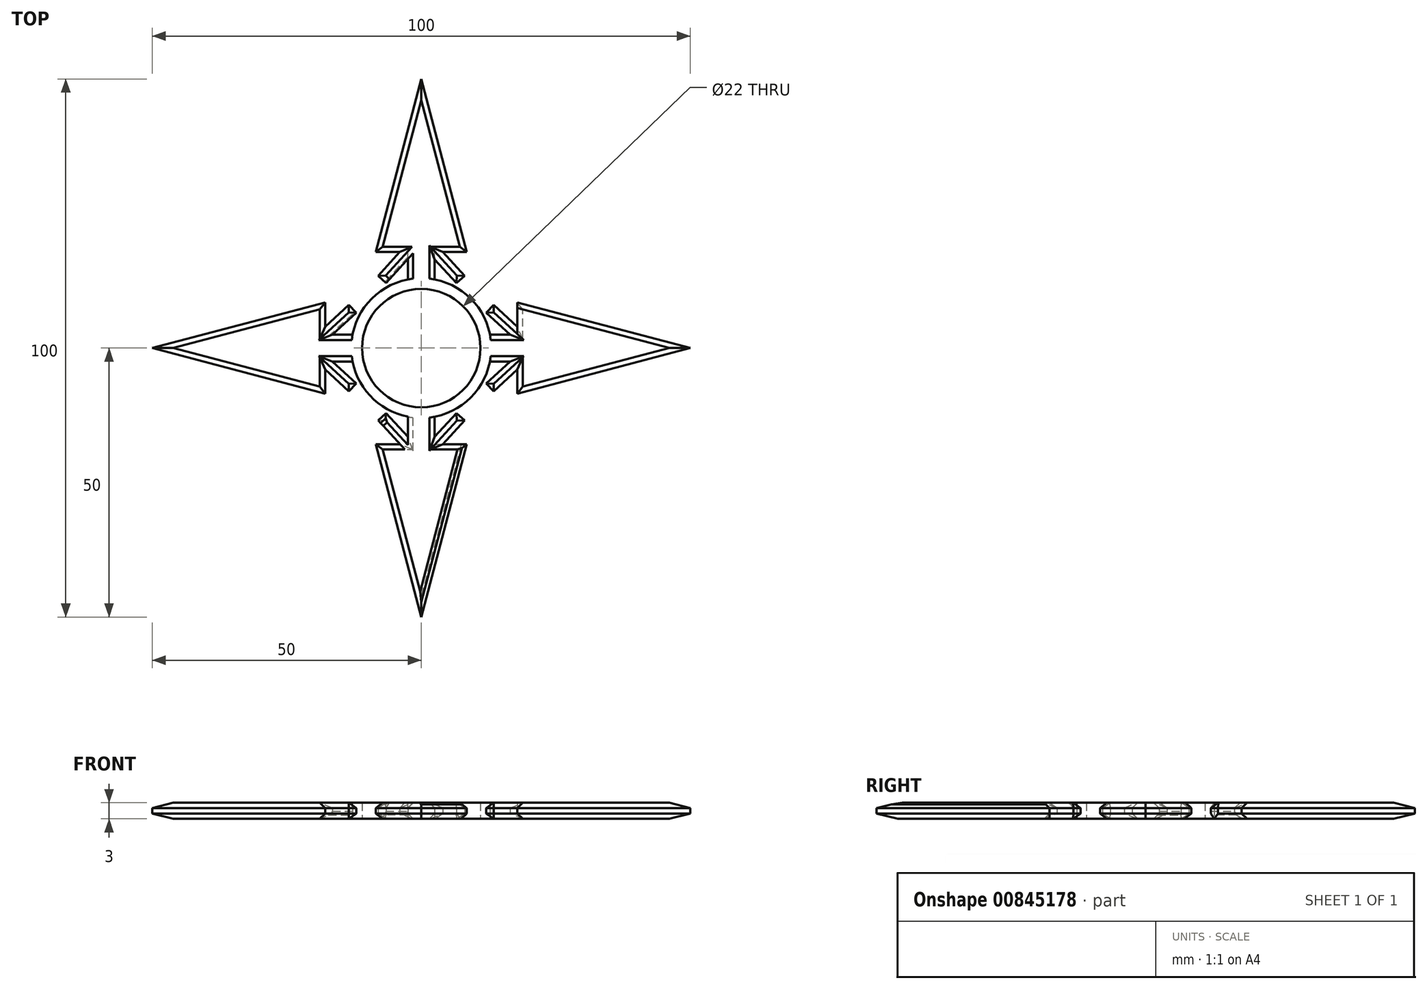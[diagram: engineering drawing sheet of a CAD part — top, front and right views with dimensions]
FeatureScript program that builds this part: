
annotation { "Feature Type Name" : "Feature", "Feature Type Description" : "" }
export const myFeature = defineFeature(function(context is Context, id is Id, definition is map)
    precondition{}
    {
        {
            var Q0;
            Q0=qCreatedBy(makeId("Top.planeOp"),FACE);
            var sketch = newSketch(context, id + "F0", { "sketchPlane" : qUnion([Q0])});
            skArc(sketch, "E0", {"start": v(7.78, 7.78) * mm, "mid": v(0, 11) * mm, "end": v(-7.78, 7.78) * mm});
            skArc(sketch, "E1", {"start": v(9.2, 9.2) * mm, "mid": v(6.11, 11.47) * mm, "end": v(2.5, 12.76) * mm});
            skLineSegment(sketch, "E2", {"start": v(0, 0) * mm, "end": v(0, 50) * mm});
            skLineSegment(sketch, "E3", {"start": v(0, 0) * mm, "end": v(-2.5, 0) * mm});
            skLineSegment(sketch, "E4", {"start": v(0, 0) * mm, "end": v(2.5, 0) * mm});
            skLineSegment(sketch, "E5", {"start": v(-2.5, 12.76) * mm, "end": v(-2.5, 16.5) * mm});
            skLineSegment(sketch, "E6", {"start": v(2.5, 12.76) * mm, "end": v(2.5, 16.5) * mm});
            skLineSegment(sketch, "E7", {"start": v(-2.5, 16.5) * mm, "end": v(-6.56, 12.08) * mm});
            skLineSegment(sketch, "E8", {"start": v(-6.56, 12.08) * mm, "end": v(-8.03, 13.43) * mm});
            skLineSegment(sketch, "E9", {"start": v(-8.03, 13.43) * mm, "end": v(-3.97, 17.85) * mm});
            skLineSegment(sketch, "E10", {"start": v(-3.97, 17.85) * mm, "end": v(-8.47, 17.85) * mm});
            skLineSegment(sketch, "E11", {"start": v(-8.47, 17.85) * mm, "end": v(0, 50) * mm});
            skLineSegment(sketch, "E12.MirrorCS", {"start": v(2.5, 16.5) * mm, "end": v(6.56, 12.08) * mm});
            skLineSegment(sketch, "E13.MirrorCS", {"start": v(8.03, 13.43) * mm, "end": v(3.97, 17.85) * mm});
            skLineSegment(sketch, "E14.MirrorCS", {"start": v(6.56, 12.08) * mm, "end": v(8.03, 13.43) * mm});
            skLineSegment(sketch, "E15.MirrorCS", {"start": v(3.97, 17.85) * mm, "end": v(8.47, 17.85) * mm});
            skLineSegment(sketch, "E16.MirrorCS", {"start": v(8.47, 17.85) * mm, "end": v(0, 50) * mm});
            skArc(sketch, "E17.trimOffspring", {"start": v(-2.5, 12.76) * mm, "mid": v(-6.11, 11.47) * mm, "end": v(-9.2, 9.2) * mm});
            skLineSegment(sketch, "E18.1.0", {"start": v(-13.43, 8.03) * mm, "end": v(-17.85, 3.97) * mm});
            skLineSegment(sketch, "E18.1.1", {"start": v(-17.85, 3.97) * mm, "end": v(-17.85, 8.47) * mm});
            skLineSegment(sketch, "E18.1.2", {"start": v(0, 0) * mm, "end": v(-50, 0) * mm});
            skArc(sketch, "E18.1.3", {"start": v(-7.78, 7.78) * mm, "mid": v(-11, 0) * mm, "end": v(-7.78, -7.78) * mm});
            skLineSegment(sketch, "E18.1.4", {"start": v(-17.85, -3.97) * mm, "end": v(-17.85, -8.47) * mm});
            skLineSegment(sketch, "E18.1.5", {"start": v(-17.85, -8.47) * mm, "end": v(-50, 0) * mm});
            skLineSegment(sketch, "E18.1.6", {"start": v(-16.5, 2.5) * mm, "end": v(-12.08, 6.56) * mm});
            skLineSegment(sketch, "E18.1.7", {"start": v(-17.85, 8.47) * mm, "end": v(-50, 0) * mm});
            skArc(sketch, "E18.1.8", {"start": v(-9.2, 9.2) * mm, "mid": v(-11.47, 6.11) * mm, "end": v(-12.76, 2.5) * mm});
            skLineSegment(sketch, "E18.1.9", {"start": v(0, 0) * mm, "end": v(0, -2.5) * mm});
            skLineSegment(sketch, "E18.1.10", {"start": v(0, 0) * mm, "end": v(0, 2.5) * mm});
            skArc(sketch, "E18.1.11", {"start": v(-12.76, -2.5) * mm, "mid": v(-11.47, -6.11) * mm, "end": v(-9.2, -9.2) * mm});
            skLineSegment(sketch, "E18.1.12", {"start": v(-13.43, -8.03) * mm, "end": v(-17.85, -3.97) * mm});
            skLineSegment(sketch, "E18.1.13", {"start": v(-16.5, -2.5) * mm, "end": v(-12.08, -6.56) * mm});
            skLineSegment(sketch, "E18.1.14", {"start": v(-12.08, 6.56) * mm, "end": v(-13.43, 8.03) * mm});
            skLineSegment(sketch, "E18.1.15", {"start": v(-12.76, 2.5) * mm, "end": v(-16.5, 2.5) * mm});
            skLineSegment(sketch, "E18.1.16", {"start": v(-12.08, -6.56) * mm, "end": v(-13.43, -8.03) * mm});
            skLineSegment(sketch, "E18.1.17", {"start": v(-12.76, -2.5) * mm, "end": v(-16.5, -2.5) * mm});
            skLineSegment(sketch, "E18.2.0", {"start": v(-8.03, -13.43) * mm, "end": v(-3.97, -17.85) * mm});
            skLineSegment(sketch, "E18.2.1", {"start": v(-3.97, -17.85) * mm, "end": v(-8.47, -17.85) * mm});
            skLineSegment(sketch, "E18.2.2", {"start": v(0, 0) * mm, "end": v(0, -50) * mm});
            skArc(sketch, "E18.2.3", {"start": v(-7.78, -7.78) * mm, "mid": v(0, -11) * mm, "end": v(7.78, -7.78) * mm});
            skLineSegment(sketch, "E18.2.4", {"start": v(3.97, -17.85) * mm, "end": v(8.47, -17.85) * mm});
            skLineSegment(sketch, "E18.2.5", {"start": v(8.47, -17.85) * mm, "end": v(0, -50) * mm});
            skLineSegment(sketch, "E18.2.6", {"start": v(-2.5, -16.5) * mm, "end": v(-6.56, -12.08) * mm});
            skLineSegment(sketch, "E18.2.7", {"start": v(-8.47, -17.85) * mm, "end": v(0, -50) * mm});
            skArc(sketch, "E18.2.8", {"start": v(-9.2, -9.2) * mm, "mid": v(-6.11, -11.47) * mm, "end": v(-2.5, -12.76) * mm});
            skArc(sketch, "E18.2.11", {"start": v(2.5, -12.76) * mm, "mid": v(6.11, -11.47) * mm, "end": v(9.2, -9.2) * mm});
            skLineSegment(sketch, "E18.2.12", {"start": v(8.03, -13.43) * mm, "end": v(3.97, -17.85) * mm});
            skLineSegment(sketch, "E18.2.13", {"start": v(2.5, -16.5) * mm, "end": v(6.56, -12.08) * mm});
            skLineSegment(sketch, "E18.2.14", {"start": v(-6.56, -12.08) * mm, "end": v(-8.03, -13.43) * mm});
            skLineSegment(sketch, "E18.2.15", {"start": v(-2.5, -12.76) * mm, "end": v(-2.5, -16.5) * mm});
            skLineSegment(sketch, "E18.2.16", {"start": v(6.56, -12.08) * mm, "end": v(8.03, -13.43) * mm});
            skLineSegment(sketch, "E18.2.17", {"start": v(2.5, -12.76) * mm, "end": v(2.5, -16.5) * mm});
            skLineSegment(sketch, "E18.3.0", {"start": v(13.43, -8.03) * mm, "end": v(17.85, -3.97) * mm});
            skLineSegment(sketch, "E18.3.1", {"start": v(17.85, -3.97) * mm, "end": v(17.85, -8.47) * mm});
            skLineSegment(sketch, "E18.3.2", {"start": v(0, 0) * mm, "end": v(50, 0) * mm});
            skArc(sketch, "E18.3.3", {"start": v(7.78, -7.78) * mm, "mid": v(11, 0) * mm, "end": v(7.78, 7.78) * mm});
            skLineSegment(sketch, "E18.3.4", {"start": v(17.85, 3.97) * mm, "end": v(17.85, 8.47) * mm});
            skLineSegment(sketch, "E18.3.5", {"start": v(17.85, 8.47) * mm, "end": v(50, 0) * mm});
            skLineSegment(sketch, "E18.3.6", {"start": v(16.5, -2.5) * mm, "end": v(12.08, -6.56) * mm});
            skLineSegment(sketch, "E18.3.7", {"start": v(17.85, -8.47) * mm, "end": v(50, 0) * mm});
            skArc(sketch, "E18.3.8", {"start": v(9.2, -9.2) * mm, "mid": v(11.47, -6.11) * mm, "end": v(12.76, -2.5) * mm});
            skLineSegment(sketch, "E18.3.9", {"start": v(0, 0) * mm, "end": v(0, 2.5) * mm});
            skLineSegment(sketch, "E18.3.10", {"start": v(0, 0) * mm, "end": v(0, -2.5) * mm});
            skArc(sketch, "E18.3.11", {"start": v(12.76, 2.5) * mm, "mid": v(11.47, 6.11) * mm, "end": v(9.2, 9.2) * mm});
            skLineSegment(sketch, "E18.3.12", {"start": v(13.43, 8.03) * mm, "end": v(17.85, 3.97) * mm});
            skLineSegment(sketch, "E18.3.13", {"start": v(16.5, 2.5) * mm, "end": v(12.08, 6.56) * mm});
            skLineSegment(sketch, "E18.3.14", {"start": v(12.08, -6.56) * mm, "end": v(13.43, -8.03) * mm});
            skLineSegment(sketch, "E18.3.15", {"start": v(12.76, -2.5) * mm, "end": v(16.5, -2.5) * mm});
            skLineSegment(sketch, "E18.3.16", {"start": v(12.08, 6.56) * mm, "end": v(13.43, 8.03) * mm});
            skLineSegment(sketch, "E18.3.17", {"start": v(12.76, 2.5) * mm, "end": v(16.5, 2.5) * mm});
            skSolve(sketch);
        }
        {
            var Q0;
            Q0 = qSketchRegion(id + "F0", true);
            extrude(context, id + "F1", {"entities" : qUnion([Q0]), "depth" : 3 * mm, "offsetDistance" : 25 * mm});
        }
        {
            var Q0;
            Q0=makeQuery(id+"F1.opExtrude","CAP_EDGE",EDGE,{"disambiguationData":[OSD([sQuery(id+"F0.wireOp",EDGE,"E11")])],"isStart":false});
            var Q1;
            Q1=makeQuery(id+"F1.opExtrude","CAP_EDGE",EDGE,{"disambiguationData":[OSD([sQuery(id+"F0.wireOp",EDGE,"E18.1.7")])],"isStart":false});
            var Q2;
            Q2=makeQuery(id+"F1.opExtrude","CAP_EDGE",EDGE,{"disambiguationData":[OSD([sQuery(id+"F0.wireOp",EDGE,"E18.1.5")])],"isStart":false});
            var Q3;
            Q3=makeQuery(id+"F1.opExtrude","CAP_EDGE",EDGE,{"disambiguationData":[OSD([sQuery(id+"F0.wireOp",EDGE,"E18.2.5")])],"isStart":false});
            var Q4;
            Q4=makeQuery(id+"F1.opExtrude","CAP_EDGE",EDGE,{"disambiguationData":[OSD([sQuery(id+"F0.wireOp",EDGE,"E18.2.7")])],"isStart":false});
            var Q5;
            Q5=makeQuery(id+"F1.opExtrude","CAP_EDGE",EDGE,{"disambiguationData":[OSD([sQuery(id+"F0.wireOp",EDGE,"E18.3.7")])],"isStart":false});
            var Q6;
            Q6=makeQuery(id+"F1.opExtrude","CAP_EDGE",EDGE,{"disambiguationData":[OSD([sQuery(id+"F0.wireOp",EDGE,"E18.3.5")])],"isStart":false});
            var Q7;
            Q7=makeQuery(id+"F1.opExtrude","CAP_EDGE",EDGE,{"disambiguationData":[OSD([sQuery(id+"F0.wireOp",EDGE,"E16.MirrorCS")])],"isStart":false});
            chamfer(context, id + "F2", {"entities" : qUnion([Q0, Q1, Q2, Q3, Q4, Q5, Q6, Q7]), "width" : 1 * mm, "tangentPropagation" : true});
        }
        {
            var Q0;
            Q0=makeQuery(id+"F1.opExtrude","CAP_EDGE",EDGE,{"disambiguationData":[OSD([sQuery(id+"F0.wireOp",EDGE,"E16.MirrorCS")])],"isStart":true});
            var Q1;
            Q1=makeQuery(id+"F1.opExtrude","CAP_EDGE",EDGE,{"disambiguationData":[OSD([sQuery(id+"F0.wireOp",EDGE,"E11")])],"isStart":true});
            var Q2;
            Q2=makeQuery(id+"F1.opExtrude","CAP_EDGE",EDGE,{"disambiguationData":[OSD([sQuery(id+"F0.wireOp",EDGE,"E18.3.7")])],"isStart":true});
            var Q3;
            Q3=makeQuery(id+"F1.opExtrude","CAP_EDGE",EDGE,{"disambiguationData":[OSD([sQuery(id+"F0.wireOp",EDGE,"E18.3.5")])],"isStart":true});
            var Q4;
            Q4=makeQuery(id+"F1.opExtrude","CAP_EDGE",EDGE,{"disambiguationData":[OSD([sQuery(id+"F0.wireOp",EDGE,"E18.2.5")])],"isStart":true});
            var Q5;
            Q5=makeQuery(id+"F1.opExtrude","CAP_EDGE",EDGE,{"disambiguationData":[OSD([sQuery(id+"F0.wireOp",EDGE,"E18.2.7")])],"isStart":true});
            var Q6;
            Q6=makeQuery(id+"F1.opExtrude","CAP_EDGE",EDGE,{"disambiguationData":[OSD([sQuery(id+"F0.wireOp",EDGE,"E18.1.5")])],"isStart":true});
            var Q7;
            Q7=makeQuery(id+"F1.opExtrude","CAP_EDGE",EDGE,{"disambiguationData":[OSD([sQuery(id+"F0.wireOp",EDGE,"E18.1.7")])],"isStart":true});
            var Q8;
            Q8=makeQuery(id+"F1.opExtrude","CAP_EDGE",EDGE,{"disambiguationData":[OSD([sQuery(id+"F0.wireOp",EDGE,"E13.MirrorCS")])],"isStart":true});
            var Q9;
            Q9=makeQuery(id+"F1.opExtrude","CAP_EDGE",EDGE,{"disambiguationData":[OSD([sQuery(id+"F0.wireOp",EDGE,"E12.MirrorCS")])],"isStart":true});
            var Q10;
            Q10=makeQuery(id+"F1.opExtrude","CAP_EDGE",EDGE,{"disambiguationData":[OSD([sQuery(id+"F0.wireOp",EDGE,"E7")])],"isStart":true});
            var Q11;
            Q11=makeQuery(id+"F1.opExtrude","CAP_EDGE",EDGE,{"disambiguationData":[OSD([sQuery(id+"F0.wireOp",EDGE,"E9")])],"isStart":true});
            var Q12;
            Q12=makeQuery(id+"F1.opExtrude","CAP_EDGE",EDGE,{"disambiguationData":[OSD([sQuery(id+"F0.wireOp",EDGE,"E10")])],"isStart":true});
            var Q13;
            Q13=makeQuery(id+"F1.opExtrude","CAP_EDGE",EDGE,{"disambiguationData":[OSD([sQuery(id+"F0.wireOp",EDGE,"E15.MirrorCS")])],"isStart":true});
            var Q14;
            Q14=makeQuery(id+"F1.opExtrude","CAP_EDGE",EDGE,{"disambiguationData":[OSD([sQuery(id+"F0.wireOp",EDGE,"E18.3.13")])],"isStart":true});
            var Q15;
            Q15=makeQuery(id+"F1.opExtrude","CAP_EDGE",EDGE,{"disambiguationData":[OSD([sQuery(id+"F0.wireOp",EDGE,"E18.3.12")])],"isStart":true});
            var Q16;
            Q16=makeQuery(id+"F1.opExtrude","CAP_EDGE",EDGE,{"disambiguationData":[OSD([sQuery(id+"F0.wireOp",EDGE,"E18.3.4")])],"isStart":true});
            var Q17;
            Q17=makeQuery(id+"F1.opExtrude","CAP_EDGE",EDGE,{"disambiguationData":[OSD([sQuery(id+"F0.wireOp",EDGE,"E18.3.16")])],"isStart":true});
            var Q18;
            Q18=makeQuery(id+"F1.opExtrude","CAP_EDGE",EDGE,{"disambiguationData":[OSD([sQuery(id+"F0.wireOp",EDGE,"E18.3.0")])],"isStart":true});
            var Q19;
            Q19=makeQuery(id+"F1.opExtrude","CAP_EDGE",EDGE,{"disambiguationData":[OSD([sQuery(id+"F0.wireOp",EDGE,"E18.3.1")])],"isStart":true});
            var Q20;
            Q20=makeQuery(id+"F1.opExtrude","CAP_EDGE",EDGE,{"disambiguationData":[OSD([sQuery(id+"F0.wireOp",EDGE,"E18.3.6")])],"isStart":true});
            var Q21;
            Q21=makeQuery(id+"F1.opExtrude","CAP_EDGE",EDGE,{"disambiguationData":[OSD([sQuery(id+"F0.wireOp",EDGE,"E18.3.14")])],"isStart":true});
            var Q22;
            Q22=makeQuery(id+"F1.opExtrude","CAP_EDGE",EDGE,{"disambiguationData":[OSD([sQuery(id+"F0.wireOp",EDGE,"E18.3.15")])],"isStart":true});
            var Q23;
            Q23=makeQuery(id+"F1.opExtrude","CAP_EDGE",EDGE,{"disambiguationData":[OSD([sQuery(id+"F0.wireOp",EDGE,"E18.3.17")])],"isStart":true});
            var Q24;
            Q24=makeQuery(id+"F1.opExtrude","CAP_EDGE",EDGE,{"disambiguationData":[OSD([sQuery(id+"F0.wireOp",EDGE,"E18.2.12")])],"isStart":true});
            var Q25;
            Q25=makeQuery(id+"F1.opExtrude","CAP_EDGE",EDGE,{"disambiguationData":[OSD([sQuery(id+"F0.wireOp",EDGE,"E18.2.16")])],"isStart":true});
            var Q26;
            Q26=makeQuery(id+"F1.opExtrude","CAP_EDGE",EDGE,{"disambiguationData":[OSD([sQuery(id+"F0.wireOp",EDGE,"E18.2.13")])],"isStart":true});
            var Q27;
            Q27=makeQuery(id+"F1.opExtrude","CAP_EDGE",EDGE,{"disambiguationData":[OSD([sQuery(id+"F0.wireOp",EDGE,"E18.2.17")])],"isStart":true});
            var Q28;
            Q28=makeQuery(id+"F1.opExtrude","CAP_EDGE",EDGE,{"disambiguationData":[OSD([sQuery(id+"F0.wireOp",EDGE,"E18.2.15")])],"isStart":true});
            var Q29;
            Q29=makeQuery(id+"F1.opExtrude","CAP_EDGE",EDGE,{"disambiguationData":[OSD([sQuery(id+"F0.wireOp",EDGE,"E18.2.6")])],"isStart":true});
            var Q30;
            Q30=makeQuery(id+"F1.opExtrude","CAP_EDGE",EDGE,{"disambiguationData":[OSD([sQuery(id+"F0.wireOp",EDGE,"E18.2.14")])],"isStart":true});
            var Q31;
            Q31=makeQuery(id+"F1.opExtrude","CAP_EDGE",EDGE,{"disambiguationData":[OSD([sQuery(id+"F0.wireOp",EDGE,"E18.2.0")])],"isStart":true});
            var Q32;
            Q32=makeQuery(id+"F1.opExtrude","CAP_EDGE",EDGE,{"disambiguationData":[OSD([sQuery(id+"F0.wireOp",EDGE,"E18.2.1")])],"isStart":true});
            var Q33;
            Q33=makeQuery(id+"F1.opExtrude","CAP_EDGE",EDGE,{"disambiguationData":[OSD([sQuery(id+"F0.wireOp",EDGE,"E18.1.4")])],"isStart":true});
            var Q34;
            Q34=makeQuery(id+"F1.opExtrude","CAP_EDGE",EDGE,{"disambiguationData":[OSD([sQuery(id+"F0.wireOp",EDGE,"E18.1.12")])],"isStart":true});
            var Q35;
            Q35=makeQuery(id+"F1.opExtrude","CAP_EDGE",EDGE,{"disambiguationData":[OSD([sQuery(id+"F0.wireOp",EDGE,"E18.1.16")])],"isStart":true});
            var Q36;
            Q36=makeQuery(id+"F1.opExtrude","CAP_EDGE",EDGE,{"disambiguationData":[OSD([sQuery(id+"F0.wireOp",EDGE,"E18.1.13")])],"isStart":true});
            var Q37;
            Q37=makeQuery(id+"F1.opExtrude","CAP_EDGE",EDGE,{"disambiguationData":[OSD([sQuery(id+"F0.wireOp",EDGE,"E18.1.17")])],"isStart":true});
            var Q38;
            Q38=makeQuery(id+"F1.opExtrude","CAP_EDGE",EDGE,{"disambiguationData":[OSD([sQuery(id+"F0.wireOp",EDGE,"E18.1.15")])],"isStart":true});
            var Q39;
            Q39=makeQuery(id+"F1.opExtrude","CAP_EDGE",EDGE,{"disambiguationData":[OSD([sQuery(id+"F0.wireOp",EDGE,"E18.1.6")])],"isStart":true});
            var Q40;
            Q40=makeQuery(id+"F1.opExtrude","CAP_EDGE",EDGE,{"disambiguationData":[OSD([sQuery(id+"F0.wireOp",EDGE,"E18.1.14")])],"isStart":true});
            var Q41;
            Q41=makeQuery(id+"F1.opExtrude","CAP_EDGE",EDGE,{"disambiguationData":[OSD([sQuery(id+"F0.wireOp",EDGE,"E18.1.0")])],"isStart":true});
            var Q42;
            Q42=makeQuery(id+"F1.opExtrude","CAP_EDGE",EDGE,{"disambiguationData":[OSD([sQuery(id+"F0.wireOp",EDGE,"E18.1.1")])],"isStart":true});
            chamfer(context, id + "F3", {"entities" : qUnion([Q0, Q1, Q2, Q3, Q4, Q5, Q6, Q7, Q8, Q9, Q10, Q11, Q12, Q13, Q14, Q15, Q16, Q17, Q18, Q19, Q20, Q21, Q22, Q23, Q24, Q25, Q26, Q27, Q28, Q29, Q30, Q31, Q32, Q33, Q34, Q35, Q36, Q37, Q38, Q39, Q40, Q41, Q42]), "width" : 1 * mm, "tangentPropagation" : true});
        }
        {
            var Q0;
            Q0=makeQuery(id+"F1.opExtrude","CAP_EDGE",EDGE,{"disambiguationData":[OSD([sQuery(id+"F0.wireOp",EDGE,"E18.3.1")])],"isStart":false});
            var Q1;
            Q1=makeQuery(id+"F1.opExtrude","CAP_EDGE",EDGE,{"disambiguationData":[OSD([sQuery(id+"F0.wireOp",EDGE,"E18.3.0")])],"isStart":false});
            var Q2;
            Q2=makeQuery(id+"F1.opExtrude","CAP_EDGE",EDGE,{"disambiguationData":[OSD([sQuery(id+"F0.wireOp",EDGE,"E18.3.14")])],"isStart":false});
            var Q3;
            Q3=makeQuery(id+"F1.opExtrude","CAP_EDGE",EDGE,{"disambiguationData":[OSD([sQuery(id+"F0.wireOp",EDGE,"E18.3.6")])],"isStart":false});
            var Q4;
            Q4=makeQuery(id+"F1.opExtrude","CAP_EDGE",EDGE,{"disambiguationData":[OSD([sQuery(id+"F0.wireOp",EDGE,"E18.3.15")])],"isStart":false});
            var Q5;
            Q5=makeQuery(id+"F1.opExtrude","CAP_EDGE",EDGE,{"disambiguationData":[OSD([sQuery(id+"F0.wireOp",EDGE,"E18.3.17")])],"isStart":false});
            var Q6;
            Q6=makeQuery(id+"F1.opExtrude","CAP_EDGE",EDGE,{"disambiguationData":[OSD([sQuery(id+"F0.wireOp",EDGE,"E18.3.13")])],"isStart":false});
            var Q7;
            Q7=makeQuery(id+"F1.opExtrude","CAP_EDGE",EDGE,{"disambiguationData":[OSD([sQuery(id+"F0.wireOp",EDGE,"E18.3.12")])],"isStart":false});
            var Q8;
            Q8=makeQuery(id+"F1.opExtrude","CAP_EDGE",EDGE,{"disambiguationData":[OSD([sQuery(id+"F0.wireOp",EDGE,"E18.3.16")])],"isStart":false});
            var Q9;
            Q9=makeQuery(id+"F1.opExtrude","CAP_EDGE",EDGE,{"disambiguationData":[OSD([sQuery(id+"F0.wireOp",EDGE,"E14.MirrorCS")])],"isStart":false});
            var Q10;
            Q10=makeQuery(id+"F1.opExtrude","CAP_EDGE",EDGE,{"disambiguationData":[OSD([sQuery(id+"F0.wireOp",EDGE,"E12.MirrorCS")])],"isStart":false});
            var Q11;
            Q11=makeQuery(id+"F1.opExtrude","CAP_EDGE",EDGE,{"disambiguationData":[OSD([sQuery(id+"F0.wireOp",EDGE,"E13.MirrorCS")])],"isStart":false});
            var Q12;
            Q12=makeQuery(id+"F1.opExtrude","CAP_EDGE",EDGE,{"disambiguationData":[OSD([sQuery(id+"F0.wireOp",EDGE,"E6")])],"isStart":false});
            var Q13;
            Q13=makeQuery(id+"F1.opExtrude","CAP_EDGE",EDGE,{"disambiguationData":[OSD([sQuery(id+"F0.wireOp",EDGE,"E5")])],"isStart":false});
            var Q14;
            Q14=makeQuery(id+"F1.opExtrude","CAP_EDGE",EDGE,{"disambiguationData":[OSD([sQuery(id+"F0.wireOp",EDGE,"E15.MirrorCS")])],"isStart":false});
            var Q15;
            {var subQ0=sQuery(id+"F0.wireOp",EDGE,"E7");Q15=makeQuery(id+"F3.opChamfer","BLEND_EDGE",EDGE,{"blendedFrom":[makeQuery(id+"F1.opExtrude","CAP_EDGE",EDGE,{"disambiguationData":[OSD([subQ0])],"isStart":true}),makeQuery(id+"F1.opExtrude","SWEPT_FACE",FACE,{"disambiguationData":[OSD([subQ0])]})],"blendedInto":[makeQuery(id+"F1.opExtrude","SWEPT_FACE",FACE,{"disambiguationData":[OSD([subQ0])]})]});}
            var Q16;
            Q16=makeQuery(id+"F1.opExtrude","CAP_EDGE",EDGE,{"disambiguationData":[OSD([sQuery(id+"F0.wireOp",EDGE,"E8")])],"isStart":false});
            var Q17;
            Q17=makeQuery(id+"F1.opExtrude","CAP_EDGE",EDGE,{"disambiguationData":[OSD([sQuery(id+"F0.wireOp",EDGE,"E9")])],"isStart":false});
            var Q18;
            Q18=makeQuery(id+"F1.opExtrude","CAP_EDGE",EDGE,{"disambiguationData":[OSD([sQuery(id+"F0.wireOp",EDGE,"E10")])],"isStart":false});
            var Q19;
            {var subQ0=sQuery(id+"F0.wireOp",EDGE,"E18.1.6");Q19=makeQuery(id+"F3.opChamfer","BLEND_EDGE",EDGE,{"blendedFrom":[makeQuery(id+"F1.opExtrude","CAP_EDGE",EDGE,{"disambiguationData":[OSD([subQ0])],"isStart":true}),makeQuery(id+"F1.opExtrude","SWEPT_FACE",FACE,{"disambiguationData":[OSD([subQ0])]})],"blendedInto":[makeQuery(id+"F1.opExtrude","SWEPT_FACE",FACE,{"disambiguationData":[OSD([subQ0])]})]});}
            var Q20;
            Q20=makeQuery(id+"F1.opExtrude","CAP_EDGE",EDGE,{"disambiguationData":[OSD([sQuery(id+"F0.wireOp",EDGE,"E18.1.6")])],"isStart":false});
            var Q21;
            Q21=makeQuery(id+"F1.opExtrude","CAP_EDGE",EDGE,{"disambiguationData":[OSD([sQuery(id+"F0.wireOp",EDGE,"E18.1.0")])],"isStart":false});
            var Q22;
            Q22=makeQuery(id+"F1.opExtrude","CAP_EDGE",EDGE,{"disambiguationData":[OSD([sQuery(id+"F0.wireOp",EDGE,"E18.1.1")])],"isStart":false});
            var Q23;
            Q23=makeQuery(id+"F1.opExtrude","CAP_EDGE",EDGE,{"disambiguationData":[OSD([sQuery(id+"F0.wireOp",EDGE,"E18.1.14")])],"isStart":false});
            var Q24;
            Q24=makeQuery(id+"F1.opExtrude","CAP_EDGE",EDGE,{"disambiguationData":[OSD([sQuery(id+"F0.wireOp",EDGE,"E18.1.15")])],"isStart":false});
            var Q25;
            Q25=makeQuery(id+"F1.opExtrude","CAP_EDGE",EDGE,{"disambiguationData":[OSD([sQuery(id+"F0.wireOp",EDGE,"E18.1.17")])],"isStart":false});
            var Q26;
            Q26=makeQuery(id+"F1.opExtrude","CAP_EDGE",EDGE,{"disambiguationData":[OSD([sQuery(id+"F0.wireOp",EDGE,"E18.1.13")])],"isStart":false});
            var Q27;
            Q27=makeQuery(id+"F1.opExtrude","CAP_EDGE",EDGE,{"disambiguationData":[OSD([sQuery(id+"F0.wireOp",EDGE,"E18.1.16")])],"isStart":false});
            var Q28;
            Q28=makeQuery(id+"F1.opExtrude","CAP_EDGE",EDGE,{"disambiguationData":[OSD([sQuery(id+"F0.wireOp",EDGE,"E18.1.12")])],"isStart":false});
            var Q29;
            Q29=makeQuery(id+"F1.opExtrude","CAP_EDGE",EDGE,{"disambiguationData":[OSD([sQuery(id+"F0.wireOp",EDGE,"E18.1.4")])],"isStart":false});
            var Q30;
            Q30=makeQuery(id+"F1.opExtrude","CAP_EDGE",EDGE,{"disambiguationData":[OSD([sQuery(id+"F0.wireOp",EDGE,"E18.2.6")])],"isStart":false});
            var Q31;
            Q31=makeQuery(id+"F1.opExtrude","CAP_EDGE",EDGE,{"disambiguationData":[OSD([sQuery(id+"F0.wireOp",EDGE,"E18.2.14")])],"isStart":false});
            chamfer(context, id + "F4", {"entities" : qUnion([Q0, Q1, Q2, Q3, Q4, Q5, Q6, Q7, Q8, Q9, Q10, Q11, Q12, Q13, Q14, Q15, Q16, Q17, Q18, Q19, Q20, Q21, Q22, Q23, Q24, Q25, Q26, Q27, Q28, Q29, Q30, Q31]), "width" : 1 * mm, "tangentPropagation" : true});
        }
        {
            var Q0;
            {var subQ0=sQuery(id+"F0.wireOp",EDGE,"E18.2.14");Q0=makeQuery(id+"F4.opChamfer","BLEND_EDGE",EDGE,{"blendedFrom":[makeQuery(id+"F1.opExtrude","CAP_EDGE",EDGE,{"disambiguationData":[OSD([subQ0])],"isStart":false}),makeQuery(id+"F1.opExtrude","CAP_FACE",FACE,{"disambiguationData":[OSD([sQuery(id+"F0.wireOp",EDGE,"E0"),sQuery(id+"F0.wireOp",EDGE,"E1"),sQuery(id+"F0.wireOp",EDGE,"E5"),sQuery(id+"F0.wireOp",EDGE,"E6"),sQuery(id+"F0.wireOp",EDGE,"E7"),sQuery(id+"F0.wireOp",EDGE,"E8"),sQuery(id+"F0.wireOp",EDGE,"E9"),sQuery(id+"F0.wireOp",EDGE,"E10"),sQuery(id+"F0.wireOp",EDGE,"E11"),sQuery(id+"F0.wireOp",EDGE,"E12.MirrorCS"),sQuery(id+"F0.wireOp",EDGE,"E13.MirrorCS"),sQuery(id+"F0.wireOp",EDGE,"E14.MirrorCS"),sQuery(id+"F0.wireOp",EDGE,"E15.MirrorCS"),sQuery(id+"F0.wireOp",EDGE,"E16.MirrorCS"),sQuery(id+"F0.wireOp",EDGE,"E17.trimOffspring"),sQuery(id+"F0.wireOp",EDGE,"E18.1.0"),sQuery(id+"F0.wireOp",EDGE,"E18.1.1"),sQuery(id+"F0.wireOp",EDGE,"E18.1.3"),sQuery(id+"F0.wireOp",EDGE,"E18.1.4"),sQuery(id+"F0.wireOp",EDGE,"E18.1.5"),sQuery(id+"F0.wireOp",EDGE,"E18.1.6"),sQuery(id+"F0.wireOp",EDGE,"E18.1.7"),sQuery(id+"F0.wireOp",EDGE,"E18.1.8"),sQuery(id+"F0.wireOp",EDGE,"E18.1.11"),sQuery(id+"F0.wireOp",EDGE,"E18.1.12"),sQuery(id+"F0.wireOp",EDGE,"E18.1.13"),sQuery(id+"F0.wireOp",EDGE,"E18.1.14"),sQuery(id+"F0.wireOp",EDGE,"E18.1.15"),sQuery(id+"F0.wireOp",EDGE,"E18.1.16"),sQuery(id+"F0.wireOp",EDGE,"E18.1.17"),sQuery(id+"F0.wireOp",EDGE,"E18.2.0"),sQuery(id+"F0.wireOp",EDGE,"E18.2.1"),sQuery(id+"F0.wireOp",EDGE,"E18.2.3"),sQuery(id+"F0.wireOp",EDGE,"E18.2.4"),sQuery(id+"F0.wireOp",EDGE,"E18.2.5"),sQuery(id+"F0.wireOp",EDGE,"E18.2.6"),sQuery(id+"F0.wireOp",EDGE,"E18.2.7"),sQuery(id+"F0.wireOp",EDGE,"E18.2.8"),sQuery(id+"F0.wireOp",EDGE,"E18.2.11"),sQuery(id+"F0.wireOp",EDGE,"E18.2.12"),sQuery(id+"F0.wireOp",EDGE,"E18.2.13"),subQ0,sQuery(id+"F0.wireOp",EDGE,"E18.2.15"),sQuery(id+"F0.wireOp",EDGE,"E18.2.16"),sQuery(id+"F0.wireOp",EDGE,"E18.2.17"),sQuery(id+"F0.wireOp",EDGE,"E18.3.0"),sQuery(id+"F0.wireOp",EDGE,"E18.3.1"),sQuery(id+"F0.wireOp",EDGE,"E18.3.3"),sQuery(id+"F0.wireOp",EDGE,"E18.3.4"),sQuery(id+"F0.wireOp",EDGE,"E18.3.5"),sQuery(id+"F0.wireOp",EDGE,"E18.3.6"),sQuery(id+"F0.wireOp",EDGE,"E18.3.7"),sQuery(id+"F0.wireOp",EDGE,"E18.3.8"),sQuery(id+"F0.wireOp",EDGE,"E18.3.11"),sQuery(id+"F0.wireOp",EDGE,"E18.3.12"),sQuery(id+"F0.wireOp",EDGE,"E18.3.13"),sQuery(id+"F0.wireOp",EDGE,"E18.3.14"),sQuery(id+"F0.wireOp",EDGE,"E18.3.15"),sQuery(id+"F0.wireOp",EDGE,"E18.3.16"),sQuery(id+"F0.wireOp",EDGE,"E18.3.17")])],"isStart":false})],"blendedInto":[makeQuery(id+"F1.opExtrude","CAP_FACE",FACE,{"disambiguationData":[OSD([sQuery(id+"F0.wireOp",EDGE,"E0"),sQuery(id+"F0.wireOp",EDGE,"E1"),sQuery(id+"F0.wireOp",EDGE,"E5"),sQuery(id+"F0.wireOp",EDGE,"E6"),sQuery(id+"F0.wireOp",EDGE,"E7"),sQuery(id+"F0.wireOp",EDGE,"E8"),sQuery(id+"F0.wireOp",EDGE,"E9"),sQuery(id+"F0.wireOp",EDGE,"E10"),sQuery(id+"F0.wireOp",EDGE,"E11"),sQuery(id+"F0.wireOp",EDGE,"E12.MirrorCS"),sQuery(id+"F0.wireOp",EDGE,"E13.MirrorCS"),sQuery(id+"F0.wireOp",EDGE,"E14.MirrorCS"),sQuery(id+"F0.wireOp",EDGE,"E15.MirrorCS"),sQuery(id+"F0.wireOp",EDGE,"E16.MirrorCS"),sQuery(id+"F0.wireOp",EDGE,"E17.trimOffspring"),sQuery(id+"F0.wireOp",EDGE,"E18.1.0"),sQuery(id+"F0.wireOp",EDGE,"E18.1.1"),sQuery(id+"F0.wireOp",EDGE,"E18.1.3"),sQuery(id+"F0.wireOp",EDGE,"E18.1.4"),sQuery(id+"F0.wireOp",EDGE,"E18.1.5"),sQuery(id+"F0.wireOp",EDGE,"E18.1.6"),sQuery(id+"F0.wireOp",EDGE,"E18.1.7"),sQuery(id+"F0.wireOp",EDGE,"E18.1.8"),sQuery(id+"F0.wireOp",EDGE,"E18.1.11"),sQuery(id+"F0.wireOp",EDGE,"E18.1.12"),sQuery(id+"F0.wireOp",EDGE,"E18.1.13"),sQuery(id+"F0.wireOp",EDGE,"E18.1.14"),sQuery(id+"F0.wireOp",EDGE,"E18.1.15"),sQuery(id+"F0.wireOp",EDGE,"E18.1.16"),sQuery(id+"F0.wireOp",EDGE,"E18.1.17"),sQuery(id+"F0.wireOp",EDGE,"E18.2.0"),sQuery(id+"F0.wireOp",EDGE,"E18.2.1"),sQuery(id+"F0.wireOp",EDGE,"E18.2.3"),sQuery(id+"F0.wireOp",EDGE,"E18.2.4"),sQuery(id+"F0.wireOp",EDGE,"E18.2.5"),sQuery(id+"F0.wireOp",EDGE,"E18.2.6"),sQuery(id+"F0.wireOp",EDGE,"E18.2.7"),sQuery(id+"F0.wireOp",EDGE,"E18.2.8"),sQuery(id+"F0.wireOp",EDGE,"E18.2.11"),sQuery(id+"F0.wireOp",EDGE,"E18.2.12"),sQuery(id+"F0.wireOp",EDGE,"E18.2.13"),subQ0,sQuery(id+"F0.wireOp",EDGE,"E18.2.15"),sQuery(id+"F0.wireOp",EDGE,"E18.2.16"),sQuery(id+"F0.wireOp",EDGE,"E18.2.17"),sQuery(id+"F0.wireOp",EDGE,"E18.3.0"),sQuery(id+"F0.wireOp",EDGE,"E18.3.1"),sQuery(id+"F0.wireOp",EDGE,"E18.3.3"),sQuery(id+"F0.wireOp",EDGE,"E18.3.4"),sQuery(id+"F0.wireOp",EDGE,"E18.3.5"),sQuery(id+"F0.wireOp",EDGE,"E18.3.6"),sQuery(id+"F0.wireOp",EDGE,"E18.3.7"),sQuery(id+"F0.wireOp",EDGE,"E18.3.8"),sQuery(id+"F0.wireOp",EDGE,"E18.3.11"),sQuery(id+"F0.wireOp",EDGE,"E18.3.12"),sQuery(id+"F0.wireOp",EDGE,"E18.3.13"),sQuery(id+"F0.wireOp",EDGE,"E18.3.14"),sQuery(id+"F0.wireOp",EDGE,"E18.3.15"),sQuery(id+"F0.wireOp",EDGE,"E18.3.16"),sQuery(id+"F0.wireOp",EDGE,"E18.3.17")])],"isStart":false})]});}
            var Q1;
            Q1=makeQuery(id+"F1.opExtrude","CAP_EDGE",EDGE,{"disambiguationData":[OSD([sQuery(id+"F0.wireOp",EDGE,"E18.2.16")])],"isStart":false});
            var Q2;
            Q2=makeQuery(id+"F1.opExtrude","CAP_EDGE",EDGE,{"disambiguationData":[OSD([sQuery(id+"F0.wireOp",EDGE,"E18.2.13")])],"isStart":false});
            var Q3;
            Q3=makeQuery(id+"F1.opExtrude","CAP_EDGE",EDGE,{"disambiguationData":[OSD([sQuery(id+"F0.wireOp",EDGE,"E18.2.12")])],"isStart":false});
            var Q4;
            Q4=makeQuery(id+"F1.opExtrude","CAP_EDGE",EDGE,{"disambiguationData":[OSD([sQuery(id+"F0.wireOp",EDGE,"E18.2.17")])],"isStart":false});
            var Q5;
            Q5=makeQuery(id+"F1.opExtrude","CAP_EDGE",EDGE,{"disambiguationData":[OSD([sQuery(id+"F0.wireOp",EDGE,"E18.2.4")])],"isStart":false});
            chamfer(context, id + "F5", {"entities" : qUnion([Q0, Q1, Q2, Q3, Q4, Q5]), "width" : 1 * mm, "tangentPropagation" : true});
        }
        {
            var Q0;
            Q0=makeQuery(id+"F1.opExtrude","CAP_EDGE",EDGE,{"disambiguationData":[OSD([sQuery(id+"F0.wireOp",EDGE,"E18.2.12")])],"isStart":false});
            var Q1;
            Q1=makeQuery(id+"F1.opExtrude","CAP_EDGE",EDGE,{"disambiguationData":[OSD([sQuery(id+"F0.wireOp",EDGE,"E18.2.13")])],"isStart":false});
            var Q2;
            Q2=makeQuery(id+"F1.opExtrude","CAP_EDGE",EDGE,{"disambiguationData":[OSD([sQuery(id+"F0.wireOp",EDGE,"E18.2.4")])],"isStart":false});
            var Q3;
            {var subQ0=sQuery(id+"F0.wireOp",EDGE,"E18.2.5");Q3=makeQuery(id+"F2.opChamfer","BLEND_EDGE",EDGE,{"blendedFrom":[makeQuery(id+"F1.opExtrude","CAP_EDGE",EDGE,{"disambiguationData":[OSD([subQ0])],"isStart":false}),makeQuery(id+"F1.opExtrude","CAP_FACE",FACE,{"disambiguationData":[OSD([sQuery(id+"F0.wireOp",EDGE,"E0"),sQuery(id+"F0.wireOp",EDGE,"E1"),sQuery(id+"F0.wireOp",EDGE,"E5"),sQuery(id+"F0.wireOp",EDGE,"E6"),sQuery(id+"F0.wireOp",EDGE,"E7"),sQuery(id+"F0.wireOp",EDGE,"E8"),sQuery(id+"F0.wireOp",EDGE,"E9"),sQuery(id+"F0.wireOp",EDGE,"E10"),sQuery(id+"F0.wireOp",EDGE,"E11"),sQuery(id+"F0.wireOp",EDGE,"E12.MirrorCS"),sQuery(id+"F0.wireOp",EDGE,"E13.MirrorCS"),sQuery(id+"F0.wireOp",EDGE,"E14.MirrorCS"),sQuery(id+"F0.wireOp",EDGE,"E15.MirrorCS"),sQuery(id+"F0.wireOp",EDGE,"E16.MirrorCS"),sQuery(id+"F0.wireOp",EDGE,"E17.trimOffspring"),sQuery(id+"F0.wireOp",EDGE,"E18.1.0"),sQuery(id+"F0.wireOp",EDGE,"E18.1.1"),sQuery(id+"F0.wireOp",EDGE,"E18.1.3"),sQuery(id+"F0.wireOp",EDGE,"E18.1.4"),sQuery(id+"F0.wireOp",EDGE,"E18.1.5"),sQuery(id+"F0.wireOp",EDGE,"E18.1.6"),sQuery(id+"F0.wireOp",EDGE,"E18.1.7"),sQuery(id+"F0.wireOp",EDGE,"E18.1.8"),sQuery(id+"F0.wireOp",EDGE,"E18.1.11"),sQuery(id+"F0.wireOp",EDGE,"E18.1.12"),sQuery(id+"F0.wireOp",EDGE,"E18.1.13"),sQuery(id+"F0.wireOp",EDGE,"E18.1.14"),sQuery(id+"F0.wireOp",EDGE,"E18.1.15"),sQuery(id+"F0.wireOp",EDGE,"E18.1.16"),sQuery(id+"F0.wireOp",EDGE,"E18.1.17"),sQuery(id+"F0.wireOp",EDGE,"E18.2.0"),sQuery(id+"F0.wireOp",EDGE,"E18.2.1"),sQuery(id+"F0.wireOp",EDGE,"E18.2.3"),sQuery(id+"F0.wireOp",EDGE,"E18.2.4"),subQ0,sQuery(id+"F0.wireOp",EDGE,"E18.2.6"),sQuery(id+"F0.wireOp",EDGE,"E18.2.7"),sQuery(id+"F0.wireOp",EDGE,"E18.2.8"),sQuery(id+"F0.wireOp",EDGE,"E18.2.11"),sQuery(id+"F0.wireOp",EDGE,"E18.2.12"),sQuery(id+"F0.wireOp",EDGE,"E18.2.13"),sQuery(id+"F0.wireOp",EDGE,"E18.2.14"),sQuery(id+"F0.wireOp",EDGE,"E18.2.15"),sQuery(id+"F0.wireOp",EDGE,"E18.2.16"),sQuery(id+"F0.wireOp",EDGE,"E18.2.17"),sQuery(id+"F0.wireOp",EDGE,"E18.3.0"),sQuery(id+"F0.wireOp",EDGE,"E18.3.1"),sQuery(id+"F0.wireOp",EDGE,"E18.3.3"),sQuery(id+"F0.wireOp",EDGE,"E18.3.4"),sQuery(id+"F0.wireOp",EDGE,"E18.3.5"),sQuery(id+"F0.wireOp",EDGE,"E18.3.6"),sQuery(id+"F0.wireOp",EDGE,"E18.3.7"),sQuery(id+"F0.wireOp",EDGE,"E18.3.8"),sQuery(id+"F0.wireOp",EDGE,"E18.3.11"),sQuery(id+"F0.wireOp",EDGE,"E18.3.12"),sQuery(id+"F0.wireOp",EDGE,"E18.3.13"),sQuery(id+"F0.wireOp",EDGE,"E18.3.14"),sQuery(id+"F0.wireOp",EDGE,"E18.3.15"),sQuery(id+"F0.wireOp",EDGE,"E18.3.16"),sQuery(id+"F0.wireOp",EDGE,"E18.3.17")])],"isStart":false})],"blendedInto":[makeQuery(id+"F1.opExtrude","CAP_FACE",FACE,{"disambiguationData":[OSD([sQuery(id+"F0.wireOp",EDGE,"E0"),sQuery(id+"F0.wireOp",EDGE,"E1"),sQuery(id+"F0.wireOp",EDGE,"E5"),sQuery(id+"F0.wireOp",EDGE,"E6"),sQuery(id+"F0.wireOp",EDGE,"E7"),sQuery(id+"F0.wireOp",EDGE,"E8"),sQuery(id+"F0.wireOp",EDGE,"E9"),sQuery(id+"F0.wireOp",EDGE,"E10"),sQuery(id+"F0.wireOp",EDGE,"E11"),sQuery(id+"F0.wireOp",EDGE,"E12.MirrorCS"),sQuery(id+"F0.wireOp",EDGE,"E13.MirrorCS"),sQuery(id+"F0.wireOp",EDGE,"E14.MirrorCS"),sQuery(id+"F0.wireOp",EDGE,"E15.MirrorCS"),sQuery(id+"F0.wireOp",EDGE,"E16.MirrorCS"),sQuery(id+"F0.wireOp",EDGE,"E17.trimOffspring"),sQuery(id+"F0.wireOp",EDGE,"E18.1.0"),sQuery(id+"F0.wireOp",EDGE,"E18.1.1"),sQuery(id+"F0.wireOp",EDGE,"E18.1.3"),sQuery(id+"F0.wireOp",EDGE,"E18.1.4"),sQuery(id+"F0.wireOp",EDGE,"E18.1.5"),sQuery(id+"F0.wireOp",EDGE,"E18.1.6"),sQuery(id+"F0.wireOp",EDGE,"E18.1.7"),sQuery(id+"F0.wireOp",EDGE,"E18.1.8"),sQuery(id+"F0.wireOp",EDGE,"E18.1.11"),sQuery(id+"F0.wireOp",EDGE,"E18.1.12"),sQuery(id+"F0.wireOp",EDGE,"E18.1.13"),sQuery(id+"F0.wireOp",EDGE,"E18.1.14"),sQuery(id+"F0.wireOp",EDGE,"E18.1.15"),sQuery(id+"F0.wireOp",EDGE,"E18.1.16"),sQuery(id+"F0.wireOp",EDGE,"E18.1.17"),sQuery(id+"F0.wireOp",EDGE,"E18.2.0"),sQuery(id+"F0.wireOp",EDGE,"E18.2.1"),sQuery(id+"F0.wireOp",EDGE,"E18.2.3"),sQuery(id+"F0.wireOp",EDGE,"E18.2.4"),subQ0,sQuery(id+"F0.wireOp",EDGE,"E18.2.6"),sQuery(id+"F0.wireOp",EDGE,"E18.2.7"),sQuery(id+"F0.wireOp",EDGE,"E18.2.8"),sQuery(id+"F0.wireOp",EDGE,"E18.2.11"),sQuery(id+"F0.wireOp",EDGE,"E18.2.12"),sQuery(id+"F0.wireOp",EDGE,"E18.2.13"),sQuery(id+"F0.wireOp",EDGE,"E18.2.14"),sQuery(id+"F0.wireOp",EDGE,"E18.2.15"),sQuery(id+"F0.wireOp",EDGE,"E18.2.16"),sQuery(id+"F0.wireOp",EDGE,"E18.2.17"),sQuery(id+"F0.wireOp",EDGE,"E18.3.0"),sQuery(id+"F0.wireOp",EDGE,"E18.3.1"),sQuery(id+"F0.wireOp",EDGE,"E18.3.3"),sQuery(id+"F0.wireOp",EDGE,"E18.3.4"),sQuery(id+"F0.wireOp",EDGE,"E18.3.5"),sQuery(id+"F0.wireOp",EDGE,"E18.3.6"),sQuery(id+"F0.wireOp",EDGE,"E18.3.7"),sQuery(id+"F0.wireOp",EDGE,"E18.3.8"),sQuery(id+"F0.wireOp",EDGE,"E18.3.11"),sQuery(id+"F0.wireOp",EDGE,"E18.3.12"),sQuery(id+"F0.wireOp",EDGE,"E18.3.13"),sQuery(id+"F0.wireOp",EDGE,"E18.3.14"),sQuery(id+"F0.wireOp",EDGE,"E18.3.15"),sQuery(id+"F0.wireOp",EDGE,"E18.3.16"),sQuery(id+"F0.wireOp",EDGE,"E18.3.17")])],"isStart":false})]});}
            var Q4;
            Q4=makeQuery(id+"F2.opChamfer","BLEND_EDGE",EDGE,{"blendedFrom":[makeQuery(id+"F1.opExtrude","CAP_EDGE",EDGE,{"disambiguationData":[OSD([sQuery(id+"F0.wireOp",EDGE,"E18.2.5")])],"isStart":false}),makeQuery(id+"F1.opExtrude","SWEPT_FACE",FACE,{"disambiguationData":[OSD([sQuery(id+"F0.wireOp",EDGE,"E18.2.4")])]})],"blendedInto":[makeQuery(id+"F1.opExtrude","SWEPT_FACE",FACE,{"disambiguationData":[OSD([sQuery(id+"F0.wireOp",EDGE,"E18.2.4")])]})]});
            chamfer(context, id + "F6", {"entities" : qUnion([Q0, Q1, Q2, Q3, Q4]), "width" : 1 * mm, "tangentPropagation" : true});
        }
        {
            var Q0;
            Q0=makeQuery(id+"F1.opExtrude","CAP_EDGE",EDGE,{"disambiguationData":[OSD([sQuery(id+"F0.wireOp",EDGE,"E18.2.1")])],"isStart":false});
            chamfer(context, id + "F7", {"entities" : qUnion([Q0]), "width" : 1 * mm, "tangentPropagation" : true});
        }
    });
